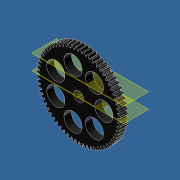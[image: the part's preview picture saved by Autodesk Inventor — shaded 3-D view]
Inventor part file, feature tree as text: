
AUTODESK INVENTOR PART (.ipt)
format: ipt  version: unknown  size: 699,904 bytes
history: native  units: in
note: dims shown in document units (in); Inventor stores cm internally (conversion verified against a paired STEP export)
features: sketch x7, extrude x6, plane x2, hole x1, other x1, projected_geometry x1
ambient origin geometry x8: Origin, YZ Plane, XZ Plane, XY Plane, X Axis, Y Axis, Z Axis, Center Point
bodies: Solid1 (feature_tree)
feature tree (18):
  extrude  "Extrusion1"  Depth=1.2205in
  extrude  "Extrusion2"  Depth=1.0in TaperAngle=0.0deg
  extrude  "Extrusion4"  Depth=0.375in TaperAngle=0.0deg
  extrude  "Extrusion5"  Depth=0.375in TaperAngle=0.0deg
  extrude  "Extrusion6"  Depth=0.2in
  plane  "Work Plane2"
  hole  "Hole2"  [1 undecoded]
  extrude  "Extrusion7"  Depth=0.625in
  sketch  "Sketch1"  dims[d0=0.185in d1=0.0in d2=1.2205in]
  sketch  "Sketch2"  dims[d3=0.185in d4=0.0in d20=1.0in d21=0.0in]
  sketch  "Sketch5"  dims[d22=0.75in d23=0.375in d24=0.0in]
  sketch  "Sketch6"  dims[d25=0.25in d26=0.375in d27=0.0in]
  sketch  "Sketch7"  dims[d28=90.0deg d29=0.2in]
  other  "Work Axis1"
  plane  "Work Plane1"
  sketch  "Sketch8"  dims[d30=0.375in]
  projected_geometry  "Projected Loop1"
  sketch  "Sketch9"  dims[d31=0.156in d32=0.75in d33=0.375in d34=0.25in d35=0.5635in d36=1.0in d37=0.8108in d38=0.45in d39=0.625in d40=2.7559in d42=360.0deg d44=1.0in d45=0.0in]
note: 1 required parameter value undecoded (feature->parameter linkage not recoverable at this tier; creation-order binding heuristic only, values carry confidence <= 0.55)
